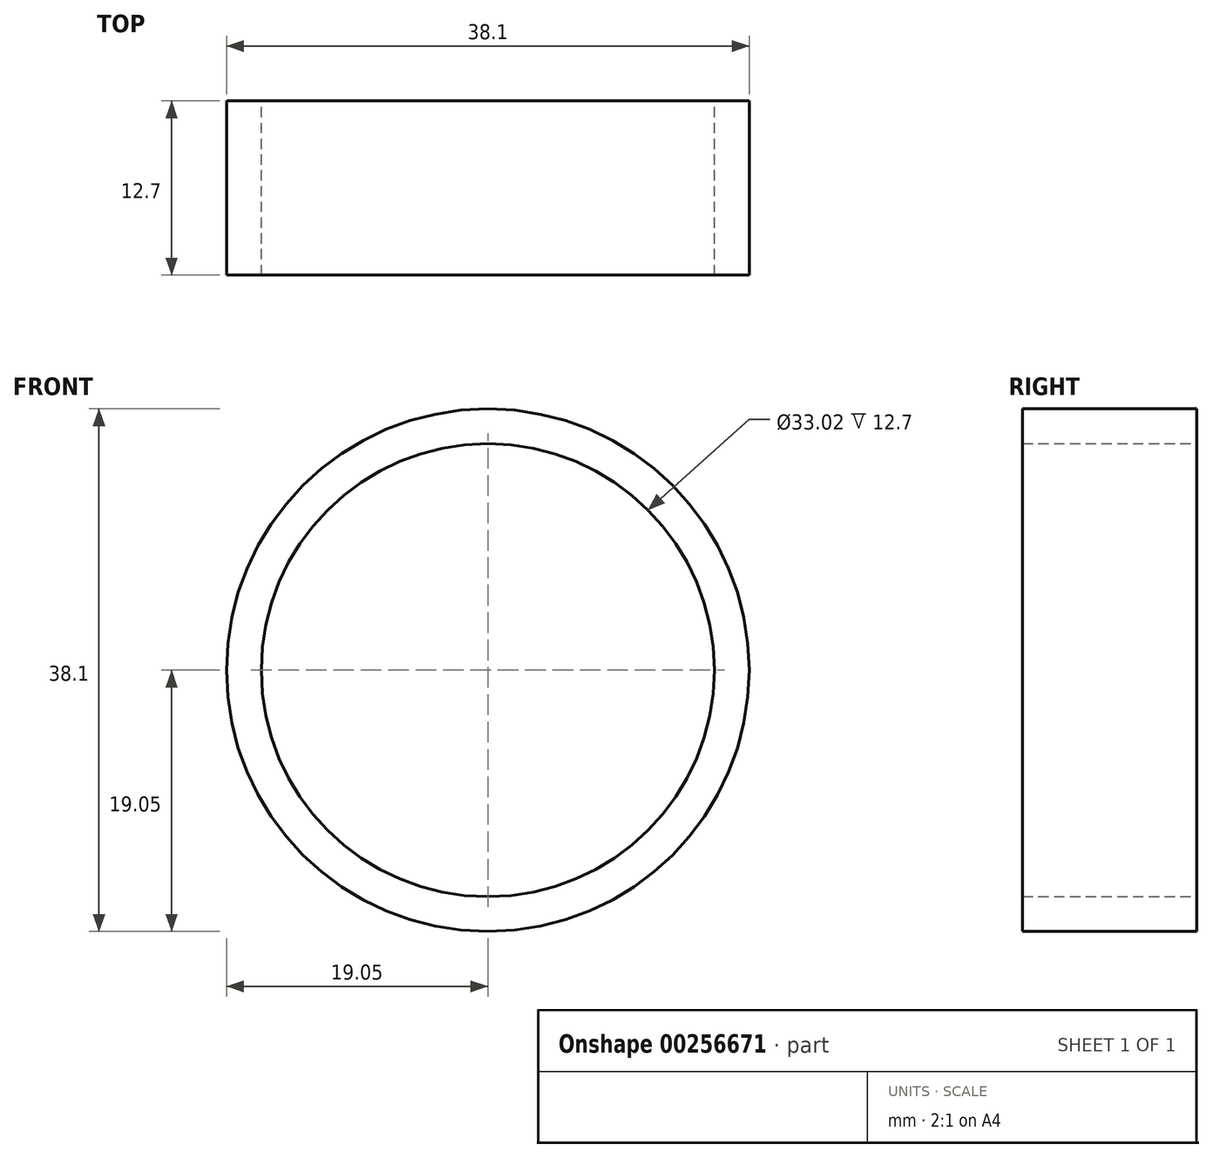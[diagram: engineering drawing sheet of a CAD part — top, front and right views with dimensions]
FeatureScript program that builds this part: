
annotation { "Feature Type Name" : "Feature", "Feature Type Description" : "" }
export const myFeature = defineFeature(function(context is Context, id is Id, definition is map)
    precondition{}
    {
        {
            var Q0;
            Q0=qCreatedBy(makeId("Front.planeOp"),FACE);
            var sketch = newSketch(context, id + "F0", { "sketchPlane" : qUnion([Q0])});
            skCircle(sketch, "E0", {"center": v(0, 0) * mm, "radius": 19.05 * mm});
            skCircle(sketch, "E1", {"center": v(0, 0) * mm, "radius": 16.51 * mm});
            skSolve(sketch);
        }
        {
            var Q0;
            Q0=makeQuery(id+"F0.imprint","IMPRINT",FACE,{"disambiguationData":[TD([[makeQuery(id+"F0.imprint","IMPRINT",EDGE,{"derivedFrom":sQuery(id+"F0.wireOp",EDGE,"E0")}),1.0]])]});
            extrude(context, id + "F1", {"entities" : qUnion([Q0]), "depth" : 12.7 * mm});
        }
    });
